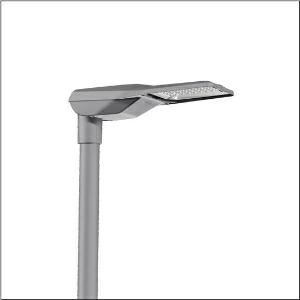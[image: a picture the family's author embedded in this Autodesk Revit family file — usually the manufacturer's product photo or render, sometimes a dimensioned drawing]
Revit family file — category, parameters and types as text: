
# Revit family: streetlight_sl_21_iq_mini___st1_0a_5xe2d31g08hb_3bda
name_source: partatom
category: Lighting Fixtures
units: mm (PartAtom-declared; Revit-internal decimal feet)

## family parameters
Cut with Voids When Loaded = No
Host = Face
Light Source = No
Part Type = Normal
Room Calculation Point = No
Round Connector Dimension = Use Diameter
Shared = No

## types (1)
- --- (1 x LED, 9450 lm, 70.9 W, 3000K)
    Apparent Load = 71 VA
    CIE Flux Codes = 37 72 97 100 100
    Color Rendering = 70
    Color Temperature = 3000K
    Default Elevation = 1800 mm
    Description = Streetlight SL 21 iQ mini, mast luminaire, primary light control with lens, of PMMA, primary optical cover: cover, of toughened safety glass, transparent, light distribution: ST1.0a, light emission: direct distribution, primary light characteristic: asymmetric, installation type: post-top, side-entry, LED, High Power LED, rated luminous flux: 9.450lm, luminous efficacy: 133lm/W, light colour: 730, colour temperature: 3000K, control: Street-Remote, Auto-Match, Temp-Guard, Lumen-Switch, Night-Set, Smart-Wire, Light-Fading, Desk-Remote (wireless, voltage-free reading and setting of iQ features in the workshop via application-optimized NFC function/RFID function), optimised constant luminous flux control (CLO 2.0), presetting dimming linear, mains connection: 220..240V, AC, 50/60Hz, start of lifetime: 71W, end of service life: 75W, reduction: 31W, luminaire housing, of diecast aluminium, powder-coated, Siteco® metallic grey (DB 702S), corrosivity category C5 mid according to DIN EN ISO 12944, please order mast flange separately, inclination adjustable: 0°, 5°, 10°, 15°, sealing non-destructively replaceable, multi-level sealing system, length: 628mm, width: 235mm, height: 110mm, mast flange for spigot size: 42mm (side-entry): 5XC10008XM4, 60/48mm (side-entry/post-top): 5XC10108XM2, 76/60mm (side-entry/post-top): 5XC10108XM1, protection rating (complete): IP66, insulation class (complete): insulation class II (safety insulation), certification: CE, ENEC, ENEC+, VDE, impact resistance: IK09, permissible operating ambient temperature for outdoor applications: -40..+50°C, standard-compliant lighting for roads and squares, packaging unit: 1 piece

Light Distribution: ST1.0a
    Height = 110 mm
    Lamp = 1 x LED
    Lamp Light Flux = 9450 lm
    Lamp Power = 70.9 W
    Lamp count = 1
    Length = 625 mm
    Luminous efficacy = 133 lm/W
    Manufacturer = Siteco
    ModVariant = No
    Model = 5XE2D31G08HB
    Number of Poles = 1
    OnlyDefault = Yes
    Power Factor = 1
    Product Name = Streetlight SL 21 iQ mini | ST1.0a
    Product group = mast luminaire | pylon top
    ProductGroupID = 6100
    Protection Class = Protection class II
    Protection Degree = IP 66
    RLX_Detail_Level = 1
    RLX_Emergency_Light_Flux = 0 lm
    RLX_Emergency_Type = 0
    RLX_Emergency_Type_DB = No
    RlxData = <blob elided: 92149 chars, md5=4f53c5ef>
    Socket = socket
    Standby Power = 0 W
    System Light Flux = 9450 lm
    System Power = 71 W
    Type Comments = factory setting: luminous flux: 100 % | dim-lin: 254 | 711 mA
    Type Image = l_1003519.jpg
    URL = http://relux.com
    VarID = @adj_090457
    Voltage = 0 V
    Weight = 0.00 kg
    Width = 234 mm

## geometry (parser evidence)
native form markers: Blend x4, Sweep x11
no freeform markers — native parametric forms only
